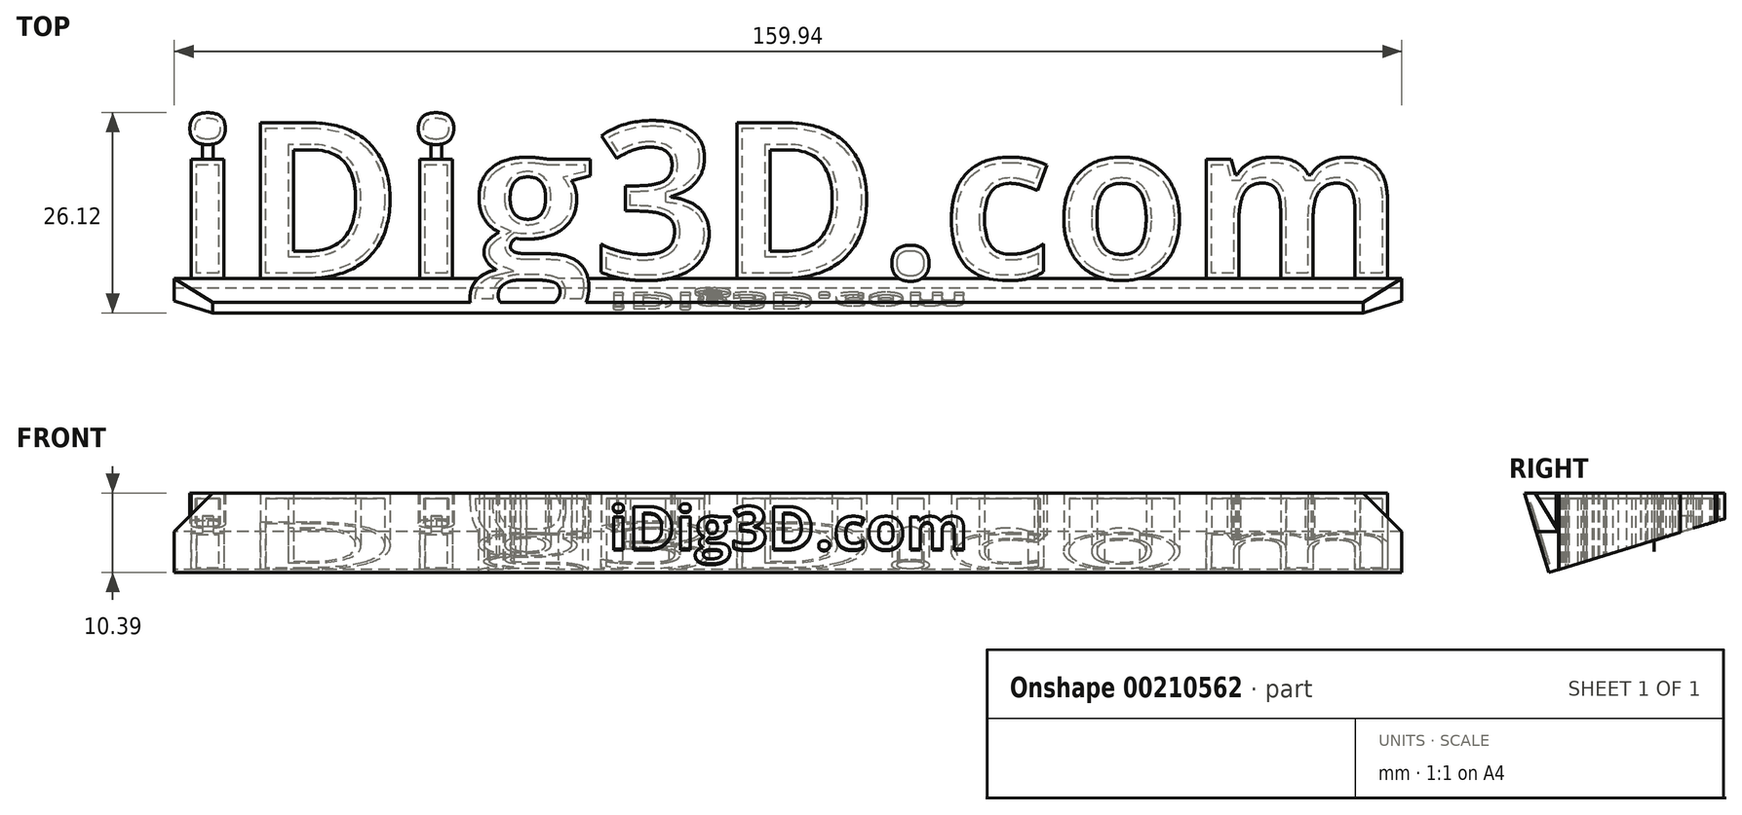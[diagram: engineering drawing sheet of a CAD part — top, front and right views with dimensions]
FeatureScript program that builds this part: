
annotation { "Feature Type Name" : "Feature", "Feature Type Description" : "" }
export const myFeature = defineFeature(function(context is Context, id is Id, definition is map)
    precondition{}
    {
        {
            var Q0;
            Q0=qCreatedBy(makeId("Top.planeOp"),FACE);
            var sketch = newSketch(context, id + "F0", { "sketchPlane" : qUnion([Q0])});
            skText(sketch, "E0", { "text": "iDig3D.com", "fontName": "OpenSans-Bold.ttf"});
            const initialGuessF0  = {"E0": [-0.08, -0.0205, 1, 0, 0.0205]};
            skSetInitialGuess(sketch, initialGuessF0);
            skSolve(sketch);
        }
        {
            var Q0;
            Q0=qSketchRegion(id+"F0",true);
            extrude(context, id + "F1", {"entities" : qUnion([Q0]), "depth" : 10 * mm});
        }
        {
            var Q0;
            Q0=makeQuery(id+"F0.imprint","IMPRINT",FACE,{"disambiguationData":[TD([[makeQuery(id+"F0.imprint","IMPRINT",EDGE,{"derivedFrom":sQuery(id+"F0.wireOp",EDGE,"E0.sketch_text.stroke-5")}),-1.0]])]});
            var sketch = newSketch(context, id + "F2", { "sketchPlane" : qUnion([Q0])});
            skPoint(sketch, "E1.0", {"position": v(-75.65, -4.96) * mm});
            skPoint(sketch, "E2.0", {"position": v(-45.88, -4.96) * mm});
            skPoint(sketch, "E3.0", {"position": v(-45.87, -3.03) * mm});
            skPoint(sketch, "E4.0", {"position": v(-75.65, -3.03) * mm});
            skLineSegment(sketch, "E5", {"start": v(-45.87, -3.03) * mm, "end": v(-45.88, -4.96) * mm});
            skLineSegment(sketch, "E6", {"start": v(-75.65, -3.03) * mm, "end": v(-75.65, -4.96) * mm});
            skArc(sketch, "E7.0.startCap", {"start": v(-46.57, -3.02) * mm, "mid": v(-45.87, -2.33) * mm, "end": v(-45.17, -3.03) * mm});
            skArc(sketch, "E7.0.endCap", {"start": v(-45.18, -4.96) * mm, "mid": v(-45.88, -5.66) * mm, "end": v(-46.58, -4.96) * mm});
            skLineSegment(sketch, "E7.0.left", {"start": v(-45.17, -3.03) * mm, "end": v(-45.18, -4.96) * mm});
            skLineSegment(sketch, "E7.0.right", {"start": v(-46.57, -3.02) * mm, "end": v(-46.58, -4.96) * mm});
            skArc(sketch, "E7.1.startCap", {"start": v(-76.35, -3.02) * mm, "mid": v(-75.64, -2.33) * mm, "end": v(-74.95, -3.03) * mm});
            skArc(sketch, "E7.1.endCap", {"start": v(-74.95, -4.96) * mm, "mid": v(-75.66, -5.66) * mm, "end": v(-76.35, -4.96) * mm});
            skLineSegment(sketch, "E7.1.left", {"start": v(-74.95, -3.03) * mm, "end": v(-74.95, -4.96) * mm});
            skLineSegment(sketch, "E7.1.right", {"start": v(-76.35, -3.02) * mm, "end": v(-76.35, -4.96) * mm});
            skSolve(sketch);
        }
        {
            var Q0;
            Q0=qSketchRegion(id+"F2",true);
            extrude(context, id + "F3", {"entities" : qUnion([Q0]), "operationType" : NewBodyOperationType.ADD, "depth" : 7 * mm});
        }
        {
            var Q0;
            Q0=makeQuery(id+"F1.opExtrude","CAP_FACE",FACE,{"disambiguationData":[OSD([sQuery(id+"F0.wireOp",EDGE,"E0.sketch_text.stroke-153"),sQuery(id+"F0.wireOp",EDGE,"E0.sketch_text.stroke-154"),sQuery(id+"F0.wireOp",EDGE,"E0.sketch_text.stroke-155"),sQuery(id+"F0.wireOp",EDGE,"E0.sketch_text.stroke-156"),sQuery(id+"F0.wireOp",EDGE,"E0.sketch_text.stroke-157"),sQuery(id+"F0.wireOp",EDGE,"E0.sketch_text.stroke-158"),sQuery(id+"F0.wireOp",EDGE,"E0.sketch_text.stroke-159"),sQuery(id+"F0.wireOp",EDGE,"E0.sketch_text.stroke-160"),sQuery(id+"F0.wireOp",EDGE,"E0.sketch_text.stroke-161"),sQuery(id+"F0.wireOp",EDGE,"E0.sketch_text.stroke-162"),sQuery(id+"F0.wireOp",EDGE,"E0.sketch_text.stroke-163"),sQuery(id+"F0.wireOp",EDGE,"E0.sketch_text.stroke-164"),sQuery(id+"F0.wireOp",EDGE,"E0.sketch_text.stroke-165"),sQuery(id+"F0.wireOp",EDGE,"E0.sketch_text.stroke-166"),sQuery(id+"F0.wireOp",EDGE,"E0.sketch_text.stroke-167"),sQuery(id+"F0.wireOp",EDGE,"E0.sketch_text.stroke-168"),sQuery(id+"F0.wireOp",EDGE,"E0.sketch_text.stroke-169"),sQuery(id+"F0.wireOp",EDGE,"E0.sketch_text.stroke-170"),sQuery(id+"F0.wireOp",EDGE,"E0.sketch_text.stroke-171"),sQuery(id+"F0.wireOp",EDGE,"E0.sketch_text.stroke-172"),sQuery(id+"F0.wireOp",EDGE,"E0.sketch_text.stroke-173"),sQuery(id+"F0.wireOp",EDGE,"E0.sketch_text.stroke-174"),sQuery(id+"F0.wireOp",EDGE,"E0.sketch_text.stroke-175"),sQuery(id+"F0.wireOp",EDGE,"E0.sketch_text.stroke-176"),sQuery(id+"F0.wireOp",EDGE,"E0.sketch_text.stroke-177"),sQuery(id+"F0.wireOp",EDGE,"E0.sketch_text.stroke-178"),sQuery(id+"F0.wireOp",EDGE,"E0.sketch_text.stroke-179"),sQuery(id+"F0.wireOp",EDGE,"E0.sketch_text.stroke-180")])],"isStart":true});
            var Q1;
            Q1=makeQuery(id+"F1.opExtrude","CAP_FACE",FACE,{"disambiguationData":[OSD([sQuery(id+"F0.wireOp",EDGE,"E0.sketch_text.stroke-30"),sQuery(id+"F0.wireOp",EDGE,"E0.sketch_text.stroke-31"),sQuery(id+"F0.wireOp",EDGE,"E0.sketch_text.stroke-32"),sQuery(id+"F0.wireOp",EDGE,"E0.sketch_text.stroke-33"),sQuery(id+"F0.wireOp",EDGE,"E0.sketch_text.stroke-34"),sQuery(id+"F0.wireOp",EDGE,"E0.sketch_text.stroke-35"),sQuery(id+"F0.wireOp",EDGE,"E0.sketch_text.stroke-36"),sQuery(id+"F0.wireOp",EDGE,"E0.sketch_text.stroke-37"),sQuery(id+"F0.wireOp",EDGE,"E0.sketch_text.stroke-38"),sQuery(id+"F0.wireOp",EDGE,"E0.sketch_text.stroke-39"),sQuery(id+"F0.wireOp",EDGE,"E0.sketch_text.stroke-40"),sQuery(id+"F0.wireOp",EDGE,"E0.sketch_text.stroke-41"),sQuery(id+"F0.wireOp",EDGE,"E0.sketch_text.stroke-42"),sQuery(id+"F0.wireOp",EDGE,"E0.sketch_text.stroke-43"),sQuery(id+"F0.wireOp",EDGE,"E0.sketch_text.stroke-44"),sQuery(id+"F0.wireOp",EDGE,"E0.sketch_text.stroke-45"),sQuery(id+"F0.wireOp",EDGE,"E0.sketch_text.stroke-46"),sQuery(id+"F0.wireOp",EDGE,"E0.sketch_text.stroke-47"),sQuery(id+"F0.wireOp",EDGE,"E0.sketch_text.stroke-48"),sQuery(id+"F0.wireOp",EDGE,"E0.sketch_text.stroke-49"),sQuery(id+"F0.wireOp",EDGE,"E0.sketch_text.stroke-50"),sQuery(id+"F0.wireOp",EDGE,"E0.sketch_text.stroke-51"),sQuery(id+"F0.wireOp",EDGE,"E0.sketch_text.stroke-52"),sQuery(id+"F0.wireOp",EDGE,"E0.sketch_text.stroke-53"),sQuery(id+"F0.wireOp",EDGE,"E0.sketch_text.stroke-54"),sQuery(id+"F0.wireOp",EDGE,"E0.sketch_text.stroke-55"),sQuery(id+"F0.wireOp",EDGE,"E0.sketch_text.stroke-56"),sQuery(id+"F0.wireOp",EDGE,"E0.sketch_text.stroke-57"),sQuery(id+"F0.wireOp",EDGE,"E0.sketch_text.stroke-58"),sQuery(id+"F0.wireOp",EDGE,"E0.sketch_text.stroke-59"),sQuery(id+"F0.wireOp",EDGE,"E0.sketch_text.stroke-60"),sQuery(id+"F0.wireOp",EDGE,"E0.sketch_text.stroke-61"),sQuery(id+"F0.wireOp",EDGE,"E0.sketch_text.stroke-62"),sQuery(id+"F0.wireOp",EDGE,"E0.sketch_text.stroke-63"),sQuery(id+"F0.wireOp",EDGE,"E0.sketch_text.stroke-64"),sQuery(id+"F0.wireOp",EDGE,"E0.sketch_text.stroke-65"),sQuery(id+"F0.wireOp",EDGE,"E0.sketch_text.stroke-66"),sQuery(id+"F0.wireOp",EDGE,"E0.sketch_text.stroke-67"),sQuery(id+"F0.wireOp",EDGE,"E0.sketch_text.stroke-68"),sQuery(id+"F0.wireOp",EDGE,"E0.sketch_text.stroke-69"),sQuery(id+"F0.wireOp",EDGE,"E0.sketch_text.stroke-70"),sQuery(id+"F0.wireOp",EDGE,"E0.sketch_text.stroke-71"),sQuery(id+"F0.wireOp",EDGE,"E0.sketch_text.stroke-72"),sQuery(id+"F0.wireOp",EDGE,"E0.sketch_text.stroke-73")])],"isStart":true});
            var Q2;
            Q2=makeQuery(id+"F1.opExtrude","CAP_FACE",FACE,{"disambiguationData":[OSD([sQuery(id+"F0.wireOp",EDGE,"E0.sketch_text.stroke-101"),sQuery(id+"F0.wireOp",EDGE,"E0.sketch_text.stroke-102"),sQuery(id+"F0.wireOp",EDGE,"E0.sketch_text.stroke-103"),sQuery(id+"F0.wireOp",EDGE,"E0.sketch_text.stroke-104"),sQuery(id+"F0.wireOp",EDGE,"E0.sketch_text.stroke-105"),sQuery(id+"F0.wireOp",EDGE,"E0.sketch_text.stroke-106"),sQuery(id+"F0.wireOp",EDGE,"E0.sketch_text.stroke-107"),sQuery(id+"F0.wireOp",EDGE,"E0.sketch_text.stroke-108"),sQuery(id+"F0.wireOp",EDGE,"E0.sketch_text.stroke-109"),sQuery(id+"F0.wireOp",EDGE,"E0.sketch_text.stroke-110"),sQuery(id+"F0.wireOp",EDGE,"E0.sketch_text.stroke-111"),sQuery(id+"F0.wireOp",EDGE,"E0.sketch_text.stroke-112")])],"isStart":true});
            var Q3;
            Q3=makeQuery(id+"F1.opExtrude","CAP_FACE",FACE,{"disambiguationData":[OSD([sQuery(id+"F0.wireOp",EDGE,"E0.sketch_text.stroke-0"),sQuery(id+"F0.wireOp",EDGE,"E0.sketch_text.stroke-1"),sQuery(id+"F0.wireOp",EDGE,"E0.sketch_text.stroke-2"),sQuery(id+"F0.wireOp",EDGE,"E0.sketch_text.stroke-3"),sQuery(id+"F0.wireOp",EDGE,"E0.sketch_text.stroke-4")])],"isStart":true});
            var Q4;
            Q4=makeQuery(id+"F1.opExtrude","CAP_FACE",FACE,{"disambiguationData":[OSD([sQuery(id+"F0.wireOp",EDGE,"E0.sketch_text.stroke-135"),sQuery(id+"F0.wireOp",EDGE,"E0.sketch_text.stroke-136"),sQuery(id+"F0.wireOp",EDGE,"E0.sketch_text.stroke-137"),sQuery(id+"F0.wireOp",EDGE,"E0.sketch_text.stroke-138"),sQuery(id+"F0.wireOp",EDGE,"E0.sketch_text.stroke-139"),sQuery(id+"F0.wireOp",EDGE,"E0.sketch_text.stroke-140"),sQuery(id+"F0.wireOp",EDGE,"E0.sketch_text.stroke-141"),sQuery(id+"F0.wireOp",EDGE,"E0.sketch_text.stroke-142"),sQuery(id+"F0.wireOp",EDGE,"E0.sketch_text.stroke-143"),sQuery(id+"F0.wireOp",EDGE,"E0.sketch_text.stroke-144"),sQuery(id+"F0.wireOp",EDGE,"E0.sketch_text.stroke-145"),sQuery(id+"F0.wireOp",EDGE,"E0.sketch_text.stroke-146"),sQuery(id+"F0.wireOp",EDGE,"E0.sketch_text.stroke-147"),sQuery(id+"F0.wireOp",EDGE,"E0.sketch_text.stroke-148"),sQuery(id+"F0.wireOp",EDGE,"E0.sketch_text.stroke-149"),sQuery(id+"F0.wireOp",EDGE,"E0.sketch_text.stroke-150"),sQuery(id+"F0.wireOp",EDGE,"E0.sketch_text.stroke-151"),sQuery(id+"F0.wireOp",EDGE,"E0.sketch_text.stroke-152")])],"isStart":true});
            var Q5;
            Q5=makeQuery(id+"F1.opExtrude","CAP_FACE",FACE,{"disambiguationData":[OSD([sQuery(id+"F0.wireOp",EDGE,"E0.sketch_text.stroke-121"),sQuery(id+"F0.wireOp",EDGE,"E0.sketch_text.stroke-122"),sQuery(id+"F0.wireOp",EDGE,"E0.sketch_text.stroke-123"),sQuery(id+"F0.wireOp",EDGE,"E0.sketch_text.stroke-124"),sQuery(id+"F0.wireOp",EDGE,"E0.sketch_text.stroke-125"),sQuery(id+"F0.wireOp",EDGE,"E0.sketch_text.stroke-126"),sQuery(id+"F0.wireOp",EDGE,"E0.sketch_text.stroke-127"),sQuery(id+"F0.wireOp",EDGE,"E0.sketch_text.stroke-128"),sQuery(id+"F0.wireOp",EDGE,"E0.sketch_text.stroke-129"),sQuery(id+"F0.wireOp",EDGE,"E0.sketch_text.stroke-130"),sQuery(id+"F0.wireOp",EDGE,"E0.sketch_text.stroke-131"),sQuery(id+"F0.wireOp",EDGE,"E0.sketch_text.stroke-132"),sQuery(id+"F0.wireOp",EDGE,"E0.sketch_text.stroke-133"),sQuery(id+"F0.wireOp",EDGE,"E0.sketch_text.stroke-134")])],"isStart":true});
            var Q6;
            Q6=makeQuery(id+"F1.opExtrude","CAP_FACE",FACE,{"disambiguationData":[OSD([sQuery(id+"F0.wireOp",EDGE,"E0.sketch_text.stroke-74"),sQuery(id+"F0.wireOp",EDGE,"E0.sketch_text.stroke-75"),sQuery(id+"F0.wireOp",EDGE,"E0.sketch_text.stroke-76"),sQuery(id+"F0.wireOp",EDGE,"E0.sketch_text.stroke-77"),sQuery(id+"F0.wireOp",EDGE,"E0.sketch_text.stroke-78"),sQuery(id+"F0.wireOp",EDGE,"E0.sketch_text.stroke-79"),sQuery(id+"F0.wireOp",EDGE,"E0.sketch_text.stroke-80"),sQuery(id+"F0.wireOp",EDGE,"E0.sketch_text.stroke-81"),sQuery(id+"F0.wireOp",EDGE,"E0.sketch_text.stroke-82"),sQuery(id+"F0.wireOp",EDGE,"E0.sketch_text.stroke-83"),sQuery(id+"F0.wireOp",EDGE,"E0.sketch_text.stroke-84"),sQuery(id+"F0.wireOp",EDGE,"E0.sketch_text.stroke-85"),sQuery(id+"F0.wireOp",EDGE,"E0.sketch_text.stroke-86"),sQuery(id+"F0.wireOp",EDGE,"E0.sketch_text.stroke-87"),sQuery(id+"F0.wireOp",EDGE,"E0.sketch_text.stroke-88"),sQuery(id+"F0.wireOp",EDGE,"E0.sketch_text.stroke-89"),sQuery(id+"F0.wireOp",EDGE,"E0.sketch_text.stroke-90"),sQuery(id+"F0.wireOp",EDGE,"E0.sketch_text.stroke-91"),sQuery(id+"F0.wireOp",EDGE,"E0.sketch_text.stroke-92"),sQuery(id+"F0.wireOp",EDGE,"E0.sketch_text.stroke-93"),sQuery(id+"F0.wireOp",EDGE,"E0.sketch_text.stroke-94"),sQuery(id+"F0.wireOp",EDGE,"E0.sketch_text.stroke-95"),sQuery(id+"F0.wireOp",EDGE,"E0.sketch_text.stroke-96"),sQuery(id+"F0.wireOp",EDGE,"E0.sketch_text.stroke-97"),sQuery(id+"F0.wireOp",EDGE,"E0.sketch_text.stroke-98"),sQuery(id+"F0.wireOp",EDGE,"E0.sketch_text.stroke-99"),sQuery(id+"F0.wireOp",EDGE,"E0.sketch_text.stroke-100")])],"isStart":true});
            var Q7;
            Q7=makeQuery(id+"F1.opExtrude","CAP_FACE",FACE,{"disambiguationData":[OSD([sQuery(id+"F0.wireOp",EDGE,"E0.sketch_text.stroke-21"),sQuery(id+"F0.wireOp",EDGE,"E0.sketch_text.stroke-22"),sQuery(id+"F0.wireOp",EDGE,"E0.sketch_text.stroke-23"),sQuery(id+"F0.wireOp",EDGE,"E0.sketch_text.stroke-24"),sQuery(id+"F0.wireOp",EDGE,"E0.sketch_text.stroke-25")])],"isStart":true});
            var Q8;
            Q8=makeQuery(id+"F1.opExtrude","CAP_FACE",FACE,{"disambiguationData":[OSD([sQuery(id+"F0.wireOp",EDGE,"E0.sketch_text.stroke-26"),sQuery(id+"F0.wireOp",EDGE,"E0.sketch_text.stroke-27"),sQuery(id+"F0.wireOp",EDGE,"E0.sketch_text.stroke-28"),sQuery(id+"F0.wireOp",EDGE,"E0.sketch_text.stroke-29")])],"isStart":true});
            var Q9;
            Q9=makeQuery(id+"F1.opExtrude","CAP_FACE",FACE,{"disambiguationData":[OSD([sQuery(id+"F0.wireOp",EDGE,"E0.sketch_text.stroke-9"),sQuery(id+"F0.wireOp",EDGE,"E0.sketch_text.stroke-10"),sQuery(id+"F0.wireOp",EDGE,"E0.sketch_text.stroke-11"),sQuery(id+"F0.wireOp",EDGE,"E0.sketch_text.stroke-12"),sQuery(id+"F0.wireOp",EDGE,"E0.sketch_text.stroke-13"),sQuery(id+"F0.wireOp",EDGE,"E0.sketch_text.stroke-14"),sQuery(id+"F0.wireOp",EDGE,"E0.sketch_text.stroke-15"),sQuery(id+"F0.wireOp",EDGE,"E0.sketch_text.stroke-16"),sQuery(id+"F0.wireOp",EDGE,"E0.sketch_text.stroke-17"),sQuery(id+"F0.wireOp",EDGE,"E0.sketch_text.stroke-18"),sQuery(id+"F0.wireOp",EDGE,"E0.sketch_text.stroke-19"),sQuery(id+"F0.wireOp",EDGE,"E0.sketch_text.stroke-20")])],"isStart":true});
            var Q10;
            Q10=makeQuery(id+"F1.opExtrude","CAP_FACE",FACE,{"disambiguationData":[OSD([sQuery(id+"F0.wireOp",EDGE,"E0.sketch_text.stroke-5"),sQuery(id+"F0.wireOp",EDGE,"E0.sketch_text.stroke-6"),sQuery(id+"F0.wireOp",EDGE,"E0.sketch_text.stroke-7"),sQuery(id+"F0.wireOp",EDGE,"E0.sketch_text.stroke-8")])],"isStart":true});
            var Q11;
            Q11=makeQuery(id+"F1.opExtrude","CAP_FACE",FACE,{"disambiguationData":[OSD([sQuery(id+"F0.wireOp",EDGE,"E0.sketch_text.stroke-113"),sQuery(id+"F0.wireOp",EDGE,"E0.sketch_text.stroke-114"),sQuery(id+"F0.wireOp",EDGE,"E0.sketch_text.stroke-115"),sQuery(id+"F0.wireOp",EDGE,"E0.sketch_text.stroke-116"),sQuery(id+"F0.wireOp",EDGE,"E0.sketch_text.stroke-117"),sQuery(id+"F0.wireOp",EDGE,"E0.sketch_text.stroke-118"),sQuery(id+"F0.wireOp",EDGE,"E0.sketch_text.stroke-119"),sQuery(id+"F0.wireOp",EDGE,"E0.sketch_text.stroke-120")])],"isStart":true});
            shell(context, id + "F4", {"entities" : qUnion([Q0, Q1, Q2, Q3, Q4, Q5, Q6, Q7, Q8, Q9, Q10, Q11]), "thickness" : .7 * mm});
        }
        {
            var Q0;
            Q0=qCreatedBy(makeId("Right.planeOp"),FACE);
            var sketch = newSketch(context, id + "F5", { "sketchPlane" : qUnion([Q0])});
            skPoint(sketch, "E8.0", {"position": v(0, 0) * mm});
            skPoint(sketch, "E8.1", {"position": v(-20.5, 0) * mm});
            skLineSegment(sketch, "E9.0", {"start": v(1.13, 10) * mm, "end": v(1.13, 6.67) * mm});
            skLineSegment(sketch, "E10.0", {"start": v(-27.35, 10) * mm, "end": v(-27.35, 0) * mm});
            skLineSegment(sketch, "E11", {"start": v(1.13, 6.67) * mm, "end": v(1.13, 3.33) * mm});
            skLineSegment(sketch, "E12", {"start": v(1.13, 3.33) * mm, "end": v(1.13, 0) * mm});
            skLineSegment(sketch, "E13", {"start": v(1.13, 6.67) * mm, "end": v(-21.79, -0.4) * mm});
            skLineSegment(sketch, "E14", {"start": v(-20.5, 0) * mm, "end": v(-23.59, 10) * mm, "construction": true});
            skLineSegment(sketch, "E15", {"start": v(-20.5, 10) * mm, "end": v(1.13, 10) * mm});
            skLineSegment(sketch, "E16", {"start": v(-20.5, 0) * mm, "end": v(-20.5, 10) * mm});
            skLineSegment(sketch, "E17", {"start": v(-23.59, 10) * mm, "end": v(-20.5, 5) * mm});
            skLineSegment(sketch, "E18", {"start": v(-21.79, -0.4) * mm, "end": v(-24.99, 10) * mm});
            skLineSegment(sketch, "E19", {"start": v(-24.99, 10) * mm, "end": v(-23.59, 10) * mm});
            skLineSegment(sketch, "E20", {"start": v(-24.99, 10) * mm, "end": v(-27.35, 10) * mm});
            skLineSegment(sketch, "E21", {"start": v(-27.35, 0) * mm, "end": v(-21.9, 0) * mm});
            skLineSegment(sketch, "E22.trimOffspring", {"start": v(-20.5, 0) * mm, "end": v(1.13, 0) * mm});
            skSolve(sketch);
        }
        {
            var Q0;
            Q0=makeQuery(id+"F5.imprint","IMPRINT",FACE,{"disambiguationData":[TD([[makeQuery(id+"F5.imprint","IMPRINT",EDGE,{"derivedFrom":sQuery(id+"F5.wireOp",EDGE,"E11")}),-1.0]])]});
            var Q1;
            {var subQ0=sQuery(id+"F5.wireOp",EDGE,"E10.0");Q1=makeQuery(id+"F5.imprint","IMPRINT",FACE,{"disambiguationData":[TD([[makeQuery(id+"F5.imprint","IMPRINT",EDGE,{"derivedFrom":subQ0}),1.0]])]});}
            var Q2;
            Q2=makeQuery(id+"F1.opExtrude","SWEPT_FACE",FACE,{"disambiguationData":[OSD([sQuery(id+"F0.wireOp",EDGE,"d4536f9c-434f-49d7-b92b-0fbf4eb391be.sketch_text.stroke-78")])]});
            var Q3;
            Q3=sQuery(id+"F0.wireOp",VERTEX,"E0.sketch_text.left.start");
            var Q4;
            Q4=makeQuery(id+"F1.opExtrude","SWEPT_FACE",FACE,{"disambiguationData":[OSD([sQuery(id+"F0.wireOp",EDGE,"d4536f9c-434f-49d7-b92b-0fbf4eb391be.sketch_text.stroke-15")])]});
            var Q5;
            Q5=sQuery(id+"F0.wireOp",VERTEX,"E0.sketch_text.right.start");
            extrude(context, id + "F6", {"entities" : qUnion([Q0, Q1]), "operationType" : NewBodyOperationType.REMOVE, "endBound" : BoundingType.UP_TO_VERTEX, "oppositeDirection" : true, "endBoundEntityFace" : qUnion([Q2]), "endBoundEntityVertex" : qUnion([Q3]), "depth" : 25 * mm, "hasSecondDirection" : true, "secondDirectionBound" : SecondDirectionBoundingType.UP_TO_VERTEX, "secondDirectionOppositeDirection" : false, "secondDirectionBoundEntityFace" : qUnion([Q4]), "secondDirectionBoundEntityVertex" : qUnion([Q5]), "secondDirectionDepth" : 25 * mm});
        }
        {
            var Q0;
            {var subQ1=sQuery(id+"F5.wireOp",EDGE,"E17");Q0=makeQuery(id+"F5.imprint","IMPRINT",FACE,{"disambiguationData":[TD([[makeQuery(id+"F5.imprint","IMPRINT",EDGE,{"derivedFrom":subQ1}),-1.0]])]});}
            var Q1;
            Q1=sQuery(id+"F0.wireOp",VERTEX,"E0.sketch_text.right.start");
            var Q2;
            Q2=makeQuery(id+"F1.opExtrude","SWEPT_FACE",FACE,{"disambiguationData":[OSD([sQuery(id+"F0.wireOp",EDGE,"d4536f9c-434f-49d7-b92b-0fbf4eb391be.sketch_text.stroke-15")])]});
            var Q3;
            Q3=sQuery(id+"F0.wireOp",VERTEX,"E0.sketch_text.left.start");
            extrude(context, id + "F7", {"entities" : qUnion([Q0]), "operationType" : NewBodyOperationType.ADD, "endBound" : BoundingType.UP_TO_VERTEX, "endBoundEntityVertex" : qUnion([Q1]), "depth" : 25 * mm, "hasSecondDirection" : true, "secondDirectionBound" : SecondDirectionBoundingType.UP_TO_VERTEX, "secondDirectionOppositeDirection" : true, "secondDirectionBoundEntityFace" : qUnion([Q2]), "secondDirectionBoundEntityVertex" : qUnion([Q3]), "secondDirectionDepth" : 25 * mm});
        }
        {
            var Q0;
            {var subQ0=sQuery(id+"F5.wireOp",EDGE,"E18");Q0=makeQuery(id+"F7.boolean.opBoolean","MERGE",FACE,{"derivedFrom":[makeQuery(id+"F6.boolean.opBoolean","COPY",FACE,{"derivedFrom":makeQuery(id+"F6.opExtrude","SWEPT_FACE",FACE,{"disambiguationData":[OSD([subQ0])]})}),makeQuery(id+"F7.opExtrude","SWEPT_FACE",FACE,{"disambiguationData":[OSD([subQ0])]})]});}
            var sketch = newSketch(context, id + "F8", { "sketchPlane" : qUnion([Q0])});
            skText(sketch, "E23", { "text": "iDig3D.com", "fontName": "OpenSans-Bold.ttf"});
            skPoint(sketch, "E24", {"position": v(0, 6.45) * mm});
            const initialGuessF8  = {"E23": [-0.0234, 0.00912, 1, 0, 0.006]};
            skSetInitialGuess(sketch, initialGuessF8);
            skSolve(sketch);
        }
        {
            var Q0;
            Q0=qSketchRegion(id+"F8",true);
            extrude(context, id + "F9", {"entities" : qUnion([Q0]), "operationType" : NewBodyOperationType.REMOVE, "oppositeDirection" : true, "depth" : .4 * mm});
        }
        {
            var Q0;
            Q0=makeQuery(id+"F7.opExtrude","CAP_EDGE",EDGE,{"disambiguationData":[OSD([sQuery(id+"F5.wireOp",EDGE,"E19")])],"isStart":false});
            var Q1;
            Q1=makeQuery(id+"F7.opExtrude","CAP_EDGE",EDGE,{"disambiguationData":[OSD([sQuery(id+"F5.wireOp",EDGE,"E19")])],"isStart":true});
            chamfer(context, id + "F10", {"entities" : qUnion([Q0, Q1]), "width" : 5 * mm, "tangentPropagation" : true});
        }
    });
